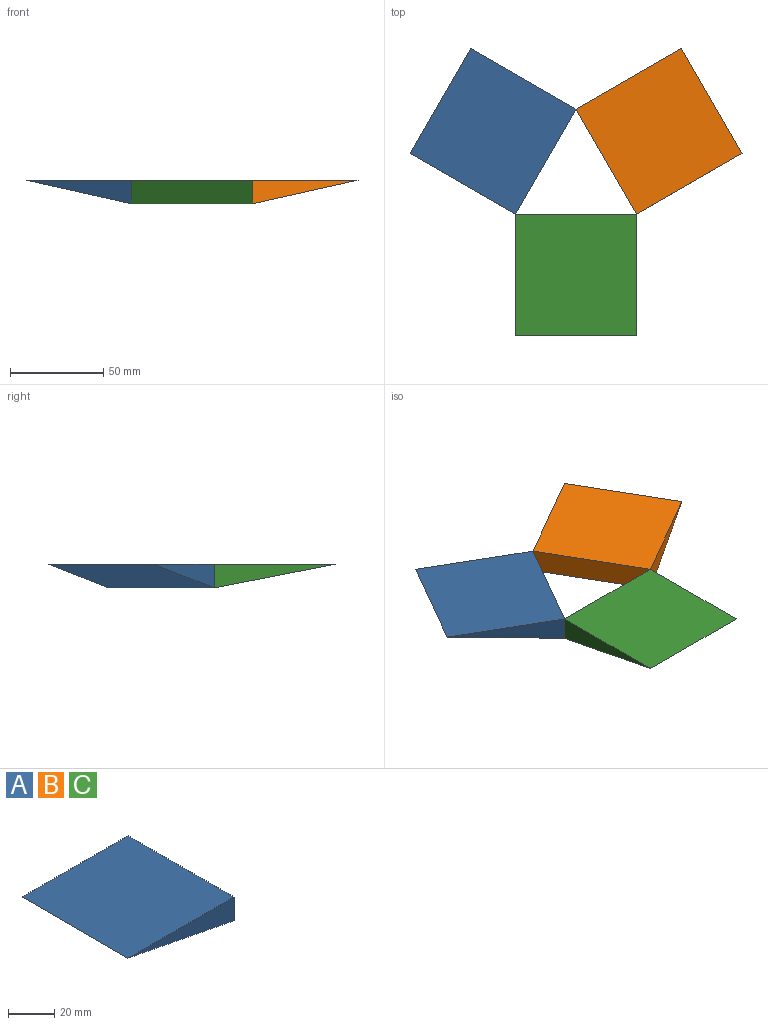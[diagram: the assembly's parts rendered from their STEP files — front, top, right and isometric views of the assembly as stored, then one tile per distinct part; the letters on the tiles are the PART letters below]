
ASSEMBLY  parts=3 mates=2
PART A: 5 faces, bbox 65x65x12.6 mm
  f0: plane 65x12.63mm, normal (1,0,0), area 821.3mm2, adj f1,f2,f3,f4
  f1: plane 65x65mm, normal (0,0,1), area 4225mm2, adj f0,f2,f3,f4
  f2: plane 65x65mm, normal (-0.19,0,-0.98), area 4304.1mm2, adj f0,f1,f3,f4
  f3: plane 65x12.63mm, normal (0,-1,0), area 410.6mm2, adj f0,f1,f2
  f4: plane 65x12.63mm, normal (0,1,0), area 410.6mm2, adj f0,f1,f2
PART B: same geometry as A
PART C: same geometry as A
PLACE A rot(axis=(0,0,-1),30deg) t=(-32.5,56.29,0)mm
PLACE B rot(axis=(0,0,-1),150deg) t=(0,0,0)mm
PLACE C rot(axis=(0,0,1),90deg) t=(-65,0,0)mm
MATE planar A.f1 <-> C.f1  axis (0,0,1) through (-76.9,44.4,0)mm
MATE planar B.f1 <-> C.f1  axis (0,0,1) through (11.9,44.4,0)mm
